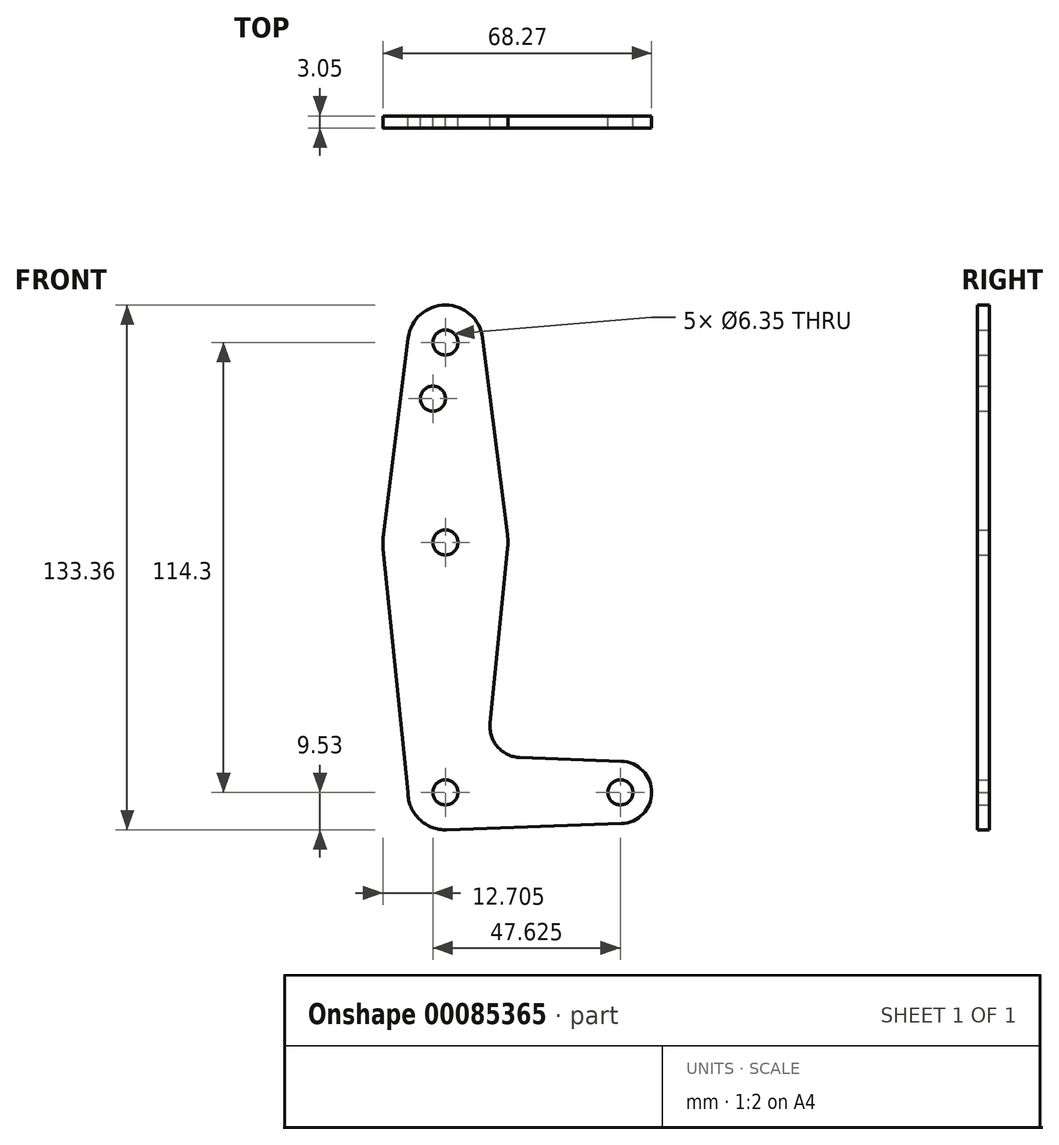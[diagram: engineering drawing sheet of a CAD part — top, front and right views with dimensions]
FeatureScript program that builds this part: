
annotation { "Feature Type Name" : "Feature", "Feature Type Description" : "" }
export const myFeature = defineFeature(function(context is Context, id is Id, definition is map)
    precondition{}
    {
        {
            var Q0;
            Q0=qCreatedBy(makeId("Front.planeOp"),FACE);
            var sketch = newSketch(context, id + "F0", { "sketchPlane" : qUnion([Q0])});
            skLineSegment(sketch, "E0", {"start": v(0, 0) * mm, "end": v(0, 114.3) * mm, "construction": true});
            skLineSegment(sketch, "E1", {"start": v(0, 0) * mm, "end": v(44.45, 0) * mm, "construction": true});
            skCircle(sketch, "E2", {"center": v(0, 0) * mm, "radius": 9.53 * mm});
            skCircle(sketch, "E3", {"center": v(0, 114.3) * mm, "radius": 9.53 * mm});
            skCircle(sketch, "E4", {"center": v(44.45, 0) * mm, "radius": 7.94 * mm});
            skCircle(sketch, "E5", {"center": v(0, 63.5) * mm, "radius": 15.88 * mm});
            skLineSegment(sketch, "E6", {"start": v(-9.52, 0) * mm, "end": v(-15.8, 61.9) * mm});
            skLineSegment(sketch, "E7", {"start": v(-15.75, 65.48) * mm, "end": v(-9.45, 115.5) * mm});
            skLineSegment(sketch, "E8", {"start": v(9.45, 115.5) * mm, "end": v(15.75, 65.48) * mm});
            skLineSegment(sketch, "E9", {"start": v(15.8, 61.91) * mm, "end": v(11.34, 17.6) * mm});
            skLineSegment(sketch, "E10", {"start": v(18.97, 8.85) * mm, "end": v(44.73, 7.93) * mm});
            skLineSegment(sketch, "E11", {"start": v(0.34, -9.52) * mm, "end": v(44.73, -7.93) * mm});
            skCircle(sketch, "E12", {"center": v(0, 114.3) * mm, "radius": 3.18 * mm});
            skCircle(sketch, "E13", {"center": v(0, 63.5) * mm, "radius": 3.18 * mm});
            skCircle(sketch, "E14", {"center": v(0, 0) * mm, "radius": 3.18 * mm});
            skCircle(sketch, "E15", {"center": v(44.45, 0) * mm, "radius": 3.18 * mm});
            skCircle(sketch, "E16", {"center": v(-3.18, 100.03) * mm, "radius": 3.18 * mm});
            skLineSegment(sketch, "E17.trimOffspring", {"start": v(9.57, 0) * mm, "end": v(9.48, -0.95) * mm});
            skPoint(sketch, "E18.visualSharp", {"position": v(10.5, 9.16) * mm});
            skArc(sketch, "E18.filletArc", {"start": v(11.34, 17.6) * mm, "mid": v(13.26, 11.57) * mm, "end": v(18.97, 8.85) * mm});
            skSolve(sketch);
        }
        {
            var Q0;
            Q0 = qSketchRegion(id + "F0", true);
            extrude(context, id + "F1", {"entities" : qUnion([Q0]), "depth" : 3.05 * mm});
        }
    });
